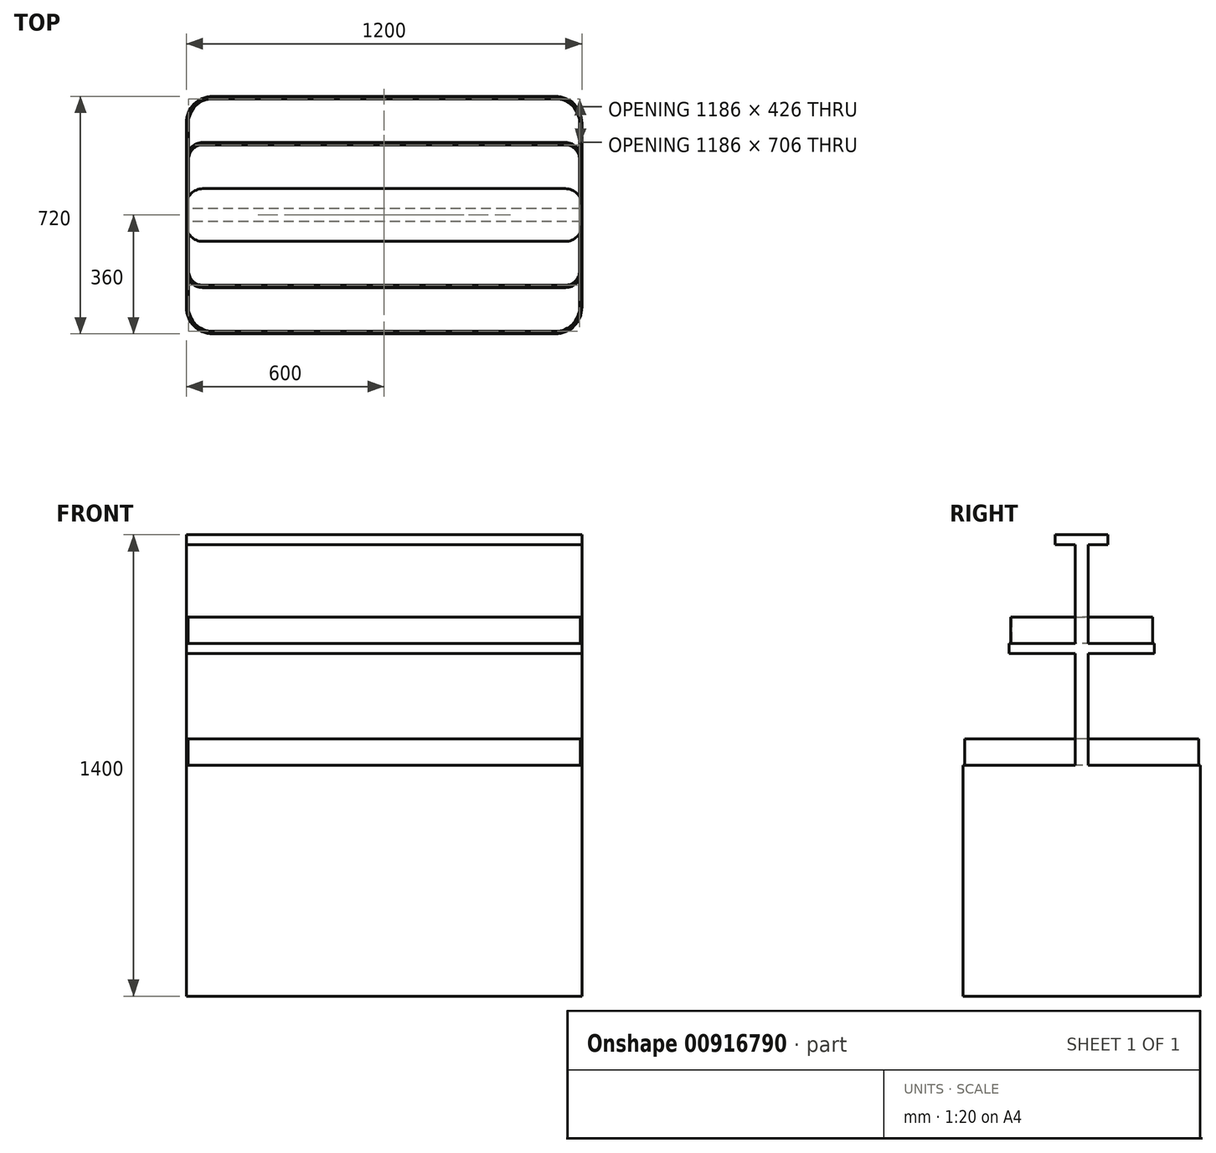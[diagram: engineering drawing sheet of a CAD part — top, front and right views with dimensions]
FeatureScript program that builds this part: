
annotation { "Feature Type Name" : "Feature", "Feature Type Description" : "" }
export const myFeature = defineFeature(function(context is Context, id is Id, definition is map)
    precondition{}
    {
        {
            var Q0;
            Q0=qCreatedBy(makeId("Front.planeOp"),FACE);
            var sketch = newSketch(context, id + "F0", { "sketchPlane" : qUnion([Q0])});
            skLineSegment(sketch, "E0.bottom", {"start": v(-600, 0) * mm, "end": v(600, 0) * mm});
            skLineSegment(sketch, "E0.top", {"start": v(-600, 1400) * mm, "end": v(600, 1400) * mm});
            skLineSegment(sketch, "E0.left", {"start": v(-600, 0) * mm, "end": v(-600, 1400) * mm});
            skLineSegment(sketch, "E0.right", {"start": v(600, 0) * mm, "end": v(600, 1400) * mm});
            skLineSegment(sketch, "E1", {"start": v(-600, 150) * mm, "end": v(600, 150) * mm});
            skLineSegment(sketch, "E2", {"start": v(-600, 700) * mm, "end": v(600, 700) * mm});
            skLineSegment(sketch, "E3", {"start": v(-600, 1370) * mm, "end": v(600, 1370) * mm});
            skLineSegment(sketch, "E4", {"start": v(-600, 1040) * mm, "end": v(600, 1040) * mm});
            skLineSegment(sketch, "E5", {"start": v(-600, 1070) * mm, "end": v(600, 1070) * mm});
            skSolve(sketch);
        }
        {
            var Q0;
            Q0=qCreatedBy(makeId("Top.planeOp"),FACE);
            var sketch = newSketch(context, id + "F1", { "sketchPlane" : qUnion([Q0])});
            skLineSegment(sketch, "E6.bottom", {"start": v(600, 360) * mm, "end": v(-600, 360) * mm});
            skLineSegment(sketch, "E6.top", {"start": v(600, -360) * mm, "end": v(-600, -360) * mm});
            skLineSegment(sketch, "E6.left", {"start": v(600, 360) * mm, "end": v(600, -360) * mm});
            skLineSegment(sketch, "E6.right", {"start": v(-600, 360) * mm, "end": v(-600, -360) * mm});
            skPoint(sketch, "E6.middle", {"position": v(0, 0) * mm});
            skLineSegment(sketch, "E7.bottom", {"start": v(600, 20) * mm, "end": v(-600, 20) * mm});
            skLineSegment(sketch, "E7.top", {"start": v(600, -20) * mm, "end": v(-600, -20) * mm});
            skLineSegment(sketch, "E7.left", {"start": v(600, 20) * mm, "end": v(600, -20) * mm});
            skLineSegment(sketch, "E7.right", {"start": v(-600, 20) * mm, "end": v(-600, -20) * mm});
            skLineSegment(sketch, "E8", {"start": v(-600, 220) * mm, "end": v(600, 220) * mm});
            skLineSegment(sketch, "E9", {"start": v(-600, -220) * mm, "end": v(600, -220) * mm});
            skLineSegment(sketch, "E10.0", {"start": v(550, 310) * mm, "end": v(-550, 310) * mm});
            skLineSegment(sketch, "E10.1", {"start": v(550, 310) * mm, "end": v(550, -310) * mm});
            skLineSegment(sketch, "E10.2", {"start": v(550, -310) * mm, "end": v(-550, -310) * mm});
            skLineSegment(sketch, "E10.3", {"start": v(-550, 310) * mm, "end": v(-550, -310) * mm});
            skLineSegment(sketch, "E11", {"start": v(-600, -80) * mm, "end": v(600, -80) * mm});
            skLineSegment(sketch, "E12", {"start": v(-600, 80) * mm, "end": v(600, 80) * mm});
            skSolve(sketch);
        }
        {
            var Q0;
            Q0=qCreatedBy(makeId("Top.planeOp"),FACE);
            var sketch = newSketch(context, id + "F2", { "sketchPlane" : qUnion([Q0])});
            skLineSegment(sketch, "E13.0", {"start": v(550, 310) * mm, "end": v(-550, 310) * mm});
            skLineSegment(sketch, "E13.1", {"start": v(-550, 310) * mm, "end": v(-550, -310) * mm});
            skLineSegment(sketch, "E13.2", {"start": v(550, -310) * mm, "end": v(-550, -310) * mm});
            skLineSegment(sketch, "E13.3", {"start": v(550, 310) * mm, "end": v(550, -310) * mm});
            skSolve(sketch);
        }
        {
            var Q0;
            Q0=qSketchRegion(id+"F2",true);
            var Q1;
            Q1=sQuery(id+"F0.wireOp",VERTEX,"E1.end");
            extrude(context, id + "F3", {"entities" : qUnion([Q0]), "endBound" : BoundingType.UP_TO_VERTEX, "depth" : 25 * mm, "endBoundEntityVertex" : qUnion([Q1]), "offsetDistance" : 25 * mm});
        }
        {
            var Q0;
            Q0=makeQuery(id+"F3.opExtrude","CAP_FACE",FACE,{"disambiguationData":[OSD([sQuery(id+"F2.wireOp",EDGE,"E13.0"),sQuery(id+"F2.wireOp",EDGE,"E13.1"),sQuery(id+"F2.wireOp",EDGE,"E13.2"),sQuery(id+"F2.wireOp",EDGE,"E13.3")])],"isStart":false});
            var sketch = newSketch(context, id + "F4", { "sketchPlane" : qUnion([Q0])});
            skLineSegment(sketch, "E14.0", {"start": v(600, 360) * mm, "end": v(-600, 360) * mm});
            skLineSegment(sketch, "E14.1", {"start": v(-600, 360) * mm, "end": v(-600, -360) * mm});
            skLineSegment(sketch, "E14.2", {"start": v(600, -360) * mm, "end": v(-600, -360) * mm});
            skLineSegment(sketch, "E14.3", {"start": v(600, 360) * mm, "end": v(600, -360) * mm});
            skSolve(sketch);
        }
        {
            var Q0;
            Q0=qSketchRegion(id+"F4",true);
            var Q1;
            Q1=sQuery(id+"F0.wireOp",VERTEX,"E2.end");
            extrude(context, id + "F5", {"entities" : qUnion([Q0]), "operationType" : NewBodyOperationType.ADD, "endBound" : BoundingType.UP_TO_VERTEX, "depth" : 25 * mm, "endBoundEntityVertex" : qUnion([Q1]), "offsetDistance" : 25 * mm});
        }
        {
            var Q0;
            Q0=makeQuery(id+"F5.opExtrude","CAP_FACE",FACE,{"disambiguationData":[OSD([sQuery(id+"F4.wireOp",EDGE,"E14.0"),sQuery(id+"F4.wireOp",EDGE,"E14.1"),sQuery(id+"F4.wireOp",EDGE,"E14.2"),sQuery(id+"F4.wireOp",EDGE,"E14.3")])],"isStart":false});
            var sketch = newSketch(context, id + "F6", { "sketchPlane" : qUnion([Q0])});
            skLineSegment(sketch, "E15.0", {"start": v(600, 20) * mm, "end": v(-600, 20) * mm});
            skLineSegment(sketch, "E15.1", {"start": v(600, -20) * mm, "end": v(-600, -20) * mm});
            skLineSegment(sketch, "E15.2", {"start": v(-600, 20) * mm, "end": v(-600, -20) * mm});
            skLineSegment(sketch, "E15.3", {"start": v(600, 20) * mm, "end": v(600, -20) * mm});
            skPoint(sketch, "E16.orphan", {"position": v(-600, 360) * mm});
            skPoint(sketch, "E17.orphan", {"position": v(-600, -360) * mm});
            skPoint(sketch, "E18.orphan", {"position": v(600, 360) * mm});
            skPoint(sketch, "E19.orphan", {"position": v(600, -360) * mm});
            skSolve(sketch);
        }
        {
            var Q0;
            Q0=qSketchRegion(id+"F6",true);
            var Q1;
            Q1=sQuery(id+"F0.wireOp",VERTEX,"E0.top.start");
            extrude(context, id + "F7", {"entities" : qUnion([Q0]), "operationType" : NewBodyOperationType.ADD, "endBound" : BoundingType.UP_TO_VERTEX, "depth" : 25 * mm, "endBoundEntityVertex" : qUnion([Q1]), "offsetDistance" : 25 * mm});
        }
        {
            var Q0;
            Q0=qCreatedBy(makeId("Top.planeOp"),FACE);
            var Q1;
            Q1=sQuery(id+"F0.wireOp",VERTEX,"E4.start");
            cPlane(context, id + "F8", {"entities" : qUnion([Q0, Q1]), "cplaneType" : CPlaneType.PLANE_POINT, "offset" : 25 * mm, "width" : 150 * mm, "height" : 150 * mm});
        }
        {
            var Q0;
            Q0=qCreatedBy(id+"F8.planeOp",FACE);
            var sketch = newSketch(context, id + "F9", { "sketchPlane" : qUnion([Q0])});
            skLineSegment(sketch, "E20.0", {"start": v(-600, 220) * mm, "end": v(600, 220) * mm});
            skLineSegment(sketch, "E20.1", {"start": v(-600, -220) * mm, "end": v(600, -220) * mm});
            skLineSegment(sketch, "E21", {"start": v(-600, 220) * mm, "end": v(-600, -220) * mm});
            skLineSegment(sketch, "E22", {"start": v(600, -220) * mm, "end": v(600, 220) * mm});
            skSolve(sketch);
        }
        {
            var Q0;
            Q0=qSketchRegion(id+"F9",true);
            var Q1;
            Q1=sQuery(id+"F0.wireOp",VERTEX,"E5.start");
            extrude(context, id + "F10", {"entities" : qUnion([Q0]), "operationType" : NewBodyOperationType.ADD, "endBound" : BoundingType.UP_TO_VERTEX, "depth" : 25 * mm, "endBoundEntityVertex" : qUnion([Q1]), "offsetDistance" : 25 * mm});
        }
        {
            var Q0;
            Q0=makeQuery(id+"F7.opExtrude","CAP_FACE",FACE,{"disambiguationData":[OSD([sQuery(id+"F6.wireOp",EDGE,"E15.0"),sQuery(id+"F6.wireOp",EDGE,"E15.1"),sQuery(id+"F6.wireOp",EDGE,"E15.2"),sQuery(id+"F6.wireOp",EDGE,"E15.3")])],"isStart":false});
            var sketch = newSketch(context, id + "F11", { "sketchPlane" : qUnion([Q0])});
            skLineSegment(sketch, "E23.0", {"start": v(-600, -80) * mm, "end": v(600, -80) * mm});
            skLineSegment(sketch, "E23.1", {"start": v(-600, 80) * mm, "end": v(600, 80) * mm});
            skLineSegment(sketch, "E24", {"start": v(-600, -80) * mm, "end": v(-600, 80) * mm});
            skLineSegment(sketch, "E25", {"start": v(600, -80) * mm, "end": v(600, 80) * mm});
            skSolve(sketch);
        }
        {
            var Q0;
            Q0=qSketchRegion(id+"F11",true);
            var Q1;
            Q1=sQuery(id+"F0.wireOp",VERTEX,"E3.start");
            extrude(context, id + "F12", {"entities" : qUnion([Q0]), "operationType" : NewBodyOperationType.ADD, "endBound" : BoundingType.UP_TO_VERTEX, "oppositeDirection" : true, "depth" : 25 * mm, "endBoundEntityVertex" : qUnion([Q1]), "offsetDistance" : 25 * mm});
        }
        {
            var Q0;
            Q0=makeQuery(id+"F5.opExtrude","SWEPT_EDGE",EDGE,{"disambiguationData":[OSD([sQuery(id+"F4.wireOp",EDGE,"E14.2"),sQuery(id+"F4.wireOp",EDGE,"E14.3")])]});
            var Q1;
            Q1=makeQuery(id+"F5.opExtrude","SWEPT_EDGE",EDGE,{"disambiguationData":[OSD([sQuery(id+"F4.wireOp",EDGE,"E14.1"),sQuery(id+"F4.wireOp",EDGE,"E14.2")])]});
            var Q2;
            Q2=makeQuery(id+"F5.opExtrude","SWEPT_EDGE",EDGE,{"disambiguationData":[OSD([sQuery(id+"F4.wireOp",EDGE,"E14.0"),sQuery(id+"F4.wireOp",EDGE,"E14.3")])]});
            var Q3;
            Q3=makeQuery(id+"F5.opExtrude","SWEPT_EDGE",EDGE,{"disambiguationData":[OSD([sQuery(id+"F4.wireOp",EDGE,"E14.0"),sQuery(id+"F4.wireOp",EDGE,"E14.1")])]});
            fillet(context, id + "F13", {"entities" : qUnion([Q0, Q1, Q2, Q3]), "radius" : 80 * mm, "tangentPropagation" : true, "allowEdgeOverflow" : false});
        }
        {
            var Q0;
            Q0=makeQuery(id+"F3.opExtrude","SWEPT_EDGE",EDGE,{"disambiguationData":[OSD([sQuery(id+"F2.wireOp",EDGE,"E13.0"),sQuery(id+"F2.wireOp",EDGE,"E13.1")])]});
            var Q1;
            Q1=makeQuery(id+"F3.opExtrude","SWEPT_EDGE",EDGE,{"disambiguationData":[OSD([sQuery(id+"F2.wireOp",EDGE,"E13.1"),sQuery(id+"F2.wireOp",EDGE,"E13.2")])]});
            var Q2;
            Q2=makeQuery(id+"F3.opExtrude","SWEPT_EDGE",EDGE,{"disambiguationData":[OSD([sQuery(id+"F2.wireOp",EDGE,"E13.2"),sQuery(id+"F2.wireOp",EDGE,"E13.3")])]});
            var Q3;
            Q3=makeQuery(id+"F3.opExtrude","SWEPT_EDGE",EDGE,{"disambiguationData":[OSD([sQuery(id+"F2.wireOp",EDGE,"E13.0"),sQuery(id+"F2.wireOp",EDGE,"E13.3")])]});
            fillet(context, id + "F14", {"entities" : qUnion([Q0, Q1, Q2, Q3]), "radius" : 85 * mm, "tangentPropagation" : true, "allowEdgeOverflow" : false});
        }
        {
            var Q0;
            Q0=makeQuery(id+"F10.opExtrude","SWEPT_EDGE",EDGE,{"disambiguationData":[OSD([sQuery(id+"F9.wireOp",EDGE,"E20.0"),sQuery(id+"F9.wireOp",EDGE,"E22")])]});
            var Q1;
            Q1=makeQuery(id+"F10.opExtrude","SWEPT_EDGE",EDGE,{"disambiguationData":[OSD([sQuery(id+"F9.wireOp",EDGE,"E20.0"),sQuery(id+"F9.wireOp",EDGE,"E21")])]});
            var Q2;
            Q2=makeQuery(id+"F10.opExtrude","SWEPT_EDGE",EDGE,{"disambiguationData":[OSD([sQuery(id+"F9.wireOp",EDGE,"E20.1"),sQuery(id+"F9.wireOp",EDGE,"E21")])]});
            var Q3;
            Q3=makeQuery(id+"F10.opExtrude","SWEPT_EDGE",EDGE,{"disambiguationData":[OSD([sQuery(id+"F9.wireOp",EDGE,"E20.1"),sQuery(id+"F9.wireOp",EDGE,"E22")])]});
            fillet(context, id + "F15", {"entities" : qUnion([Q0, Q1, Q2, Q3]), "radius" : 50 * mm, "tangentPropagation" : true, "allowEdgeOverflow" : false});
        }
        {
            var Q0;
            Q0=makeQuery(id+"F12.opExtrude","SWEPT_EDGE",EDGE,{"disambiguationData":[OSD([sQuery(id+"F11.wireOp",EDGE,"E23.0"),sQuery(id+"F11.wireOp",EDGE,"E25")])]});
            var Q1;
            Q1=makeQuery(id+"F12.opExtrude","SWEPT_EDGE",EDGE,{"disambiguationData":[OSD([sQuery(id+"F11.wireOp",EDGE,"E23.1"),sQuery(id+"F11.wireOp",EDGE,"E25")])]});
            var Q2;
            Q2=makeQuery(id+"F12.opExtrude","SWEPT_EDGE",EDGE,{"disambiguationData":[OSD([sQuery(id+"F11.wireOp",EDGE,"E23.0"),sQuery(id+"F11.wireOp",EDGE,"E24")])]});
            var Q3;
            Q3=makeQuery(id+"F12.opExtrude","SWEPT_EDGE",EDGE,{"disambiguationData":[OSD([sQuery(id+"F11.wireOp",EDGE,"E23.1"),sQuery(id+"F11.wireOp",EDGE,"E24")])]});
            fillet(context, id + "F16", {"entities" : qUnion([Q0, Q1, Q2, Q3]), "radius" : 50 * mm, "tangentPropagation" : true, "allowEdgeOverflow" : false});
        }
        {
            var Q0;
            {var subQ0=sQuery(id+"F4.wireOp",EDGE,"E14.3");var subQ1=sQuery(id+"F4.wireOp",EDGE,"E14.2");var subQ2=sQuery(id+"F4.wireOp",EDGE,"E14.1");Q0=makeQuery(id+"F7.boolean.opBoolean","SPLIT",FACE,{"disambiguationData":[TD([makeQuery(id+"F5.opExtrude","SWEPT_FACE",FACE,{"disambiguationData":[OSD([subQ1])]})])],"derivedFrom":makeQuery(id+"F5.opExtrude","CAP_FACE",FACE,{"disambiguationData":[OSD([sQuery(id+"F4.wireOp",EDGE,"E14.0"),subQ2,subQ1,subQ0])],"isStart":false})});}
            var sketch = newSketch(context, id + "F17", { "sketchPlane" : qUnion([Q0])});
            skArc(sketch, "E26.0", {"start": v(-595, 280) * mm, "mid": v(-573.03, 333.03) * mm, "end": v(-520, 355) * mm});
            skLineSegment(sketch, "E26.1", {"start": v(520, 355) * mm, "end": v(-520, 355) * mm});
            skLineSegment(sketch, "E26.2", {"start": v(-595, 280) * mm, "end": v(-595, -280) * mm});
            skArc(sketch, "E26.3", {"start": v(520, 355) * mm, "mid": v(573.03, 333.03) * mm, "end": v(595, 280) * mm});
            skArc(sketch, "E26.4", {"start": v(-520, -355) * mm, "mid": v(-573.03, -333.03) * mm, "end": v(-595, -280) * mm});
            skLineSegment(sketch, "E26.5", {"start": v(520, -355) * mm, "end": v(-520, -355) * mm});
            skArc(sketch, "E26.6", {"start": v(595, -280) * mm, "mid": v(573.03, -333.03) * mm, "end": v(520, -355) * mm});
            skLineSegment(sketch, "E26.7", {"start": v(595, 280) * mm, "end": v(595, -280) * mm});
            skLineSegment(sketch, "E27.0", {"start": v(520, -353) * mm, "end": v(-520, -353) * mm});
            skArc(sketch, "E27.1", {"start": v(593, -280) * mm, "mid": v(571.62, -331.62) * mm, "end": v(520, -353) * mm});
            skArc(sketch, "E27.2", {"start": v(-520, -353) * mm, "mid": v(-571.62, -331.62) * mm, "end": v(-593, -280) * mm});
            skLineSegment(sketch, "E27.3", {"start": v(593, 280) * mm, "end": v(593, -280) * mm});
            skLineSegment(sketch, "E27.4", {"start": v(-593, 280) * mm, "end": v(-593, -280) * mm});
            skArc(sketch, "E27.5", {"start": v(-593, 280) * mm, "mid": v(-571.62, 331.62) * mm, "end": v(-520, 353) * mm});
            skLineSegment(sketch, "E27.6", {"start": v(520, 353) * mm, "end": v(-520, 353) * mm});
            skArc(sketch, "E27.7", {"start": v(520, 353) * mm, "mid": v(571.62, 331.62) * mm, "end": v(593, 280) * mm});
            skSolve(sketch);
        }
        {
            var Q0;
            Q0=qSketchRegion(id+"F17",true);
            extrude(context, id + "F18", {"entities" : qUnion([Q0]), "depth" : 80 * mm, "offsetDistance" : 25 * mm});
        }
        {
            var Q0;
            {var subQ0=sQuery(id+"F9.wireOp",EDGE,"E20.1");var subQ1=sQuery(id+"F9.wireOp",EDGE,"E21");var subQ2=sQuery(id+"F9.wireOp",EDGE,"E22");Q0=makeQuery(id+"F10.boolean.opBoolean","SPLIT",FACE,{"disambiguationData":[TD([makeQuery(id+"F7.opExtrude","SWEPT_FACE",FACE,{"disambiguationData":[OSD([sQuery(id+"F6.wireOp",EDGE,"E15.1")])]})])],"derivedFrom":makeQuery(id+"F10.opExtrude","CAP_FACE",FACE,{"disambiguationData":[OSD([sQuery(id+"F9.wireOp",EDGE,"E20.0"),subQ0,subQ1,subQ2])],"isStart":false})});}
            var sketch = newSketch(context, id + "F19", { "sketchPlane" : qUnion([Q0])});
            skLineSegment(sketch, "E28.0", {"start": v(-595, 170) * mm, "end": v(-595, 15) * mm});
            skLineSegment(sketch, "E28.1", {"start": v(595, 15) * mm, "end": v(595, 170) * mm});
            skArc(sketch, "E28.2", {"start": v(595, 170) * mm, "mid": v(581.82, 201.82) * mm, "end": v(550, 215) * mm});
            skLineSegment(sketch, "E28.3", {"start": v(-550, 215) * mm, "end": v(550, 215) * mm});
            skArc(sketch, "E28.4", {"start": v(-550, 215) * mm, "mid": v(-581.82, 201.82) * mm, "end": v(-595, 170) * mm});
            skLineSegment(sketch, "E29.0", {"start": v(595, -170) * mm, "end": v(595, -15) * mm});
            skLineSegment(sketch, "E29.1", {"start": v(-595, -15) * mm, "end": v(-595, -170) * mm});
            skArc(sketch, "E29.2", {"start": v(-595, -170) * mm, "mid": v(-581.82, -201.82) * mm, "end": v(-550, -215) * mm});
            skLineSegment(sketch, "E29.3", {"start": v(-550, -215) * mm, "end": v(550, -215) * mm});
            skArc(sketch, "E29.4", {"start": v(550, -215) * mm, "mid": v(581.82, -201.82) * mm, "end": v(595, -170) * mm});
            skLineSegment(sketch, "E30", {"start": v(-595, 15) * mm, "end": v(-595, -15) * mm});
            skLineSegment(sketch, "E31", {"start": v(595, 15) * mm, "end": v(595, -15) * mm});
            skLineSegment(sketch, "E32.0", {"start": v(593, 15) * mm, "end": v(593, 170) * mm});
            skLineSegment(sketch, "E32.1", {"start": v(-593, 15) * mm, "end": v(-593, -15) * mm});
            skLineSegment(sketch, "E32.2", {"start": v(-593, 170) * mm, "end": v(-593, 15) * mm});
            skArc(sketch, "E32.3", {"start": v(-550, 213) * mm, "mid": v(-580.4, 200.4) * mm, "end": v(-593, 170) * mm});
            skLineSegment(sketch, "E32.4", {"start": v(-550, 213) * mm, "end": v(550, 213) * mm});
            skLineSegment(sketch, "E32.5", {"start": v(-593, -15) * mm, "end": v(-593, -170) * mm});
            skArc(sketch, "E32.6", {"start": v(593, 170) * mm, "mid": v(580.4, 200.4) * mm, "end": v(550, 213) * mm});
            skArc(sketch, "E32.7", {"start": v(-593, -170) * mm, "mid": v(-580.4, -200.4) * mm, "end": v(-550, -213) * mm});
            skLineSegment(sketch, "E32.8", {"start": v(-550, -213) * mm, "end": v(550, -213) * mm});
            skArc(sketch, "E32.9", {"start": v(550, -213) * mm, "mid": v(580.4, -200.4) * mm, "end": v(593, -170) * mm});
            skLineSegment(sketch, "E32.10", {"start": v(593, -170) * mm, "end": v(593, -15) * mm});
            skLineSegment(sketch, "E32.11", {"start": v(593, 15) * mm, "end": v(593, -15) * mm});
            skSolve(sketch);
        }
        {
            var Q0;
            Q0=qSketchRegion(id+"F19",true);
            extrude(context, id + "F20", {"entities" : qUnion([Q0]), "depth" : 80 * mm, "offsetDistance" : 25 * mm});
        }
        {
            var Q0;
            Q0=makeQuery(id+"F12.boolean.opBoolean","MERGE",FACE,{"derivedFrom":[makeQuery(id+"F10.boolean.opBoolean","MERGE",FACE,{"derivedFrom":[makeQuery(id+"F7.boolean.opBoolean","MERGE",FACE,{"derivedFrom":[makeQuery(id+"F5.opExtrude","SWEPT_FACE",FACE,{"disambiguationData":[OSD([sQuery(id+"F4.wireOp",EDGE,"E14.3")])]}),makeQuery(id+"F7.opExtrude","SWEPT_FACE",FACE,{"disambiguationData":[OSD([sQuery(id+"F6.wireOp",EDGE,"E15.3")])]})]}),makeQuery(id+"F10.opExtrude","SWEPT_FACE",FACE,{"disambiguationData":[OSD([sQuery(id+"F9.wireOp",EDGE,"E22")])]})]}),makeQuery(id+"F12.opExtrude","SWEPT_FACE",FACE,{"disambiguationData":[OSD([sQuery(id+"F11.wireOp",EDGE,"E25")])]})]});
            var sketch = newSketch(context, id + "F21", { "sketchPlane" : qUnion([Q0])});
            skLineSegment(sketch, "E33", {"start": v(0, 0) * mm, "end": v(0, 2000) * mm, "construction": true});
            skLineSegment(sketch, "E34", {"start": v(0, 2000) * mm, "end": v(-360, 1950) * mm});
            skLineSegment(sketch, "E35", {"start": v(-360, 1950) * mm, "end": v(-360, 1800) * mm});
            skLineSegment(sketch, "E36.MirrorCS", {"start": v(0, 2000) * mm, "end": v(360, 1950) * mm});
            skLineSegment(sketch, "E37.MirrorCS", {"start": v(360, 1950) * mm, "end": v(360, 1800) * mm});
            skSolve(sketch);
        }
        {
            var Q0;
            {var subQ6=sQuery(id+"F4.wireOp",EDGE,"E14.3");Q0=makeQuery(id+"F21.imprint","IMPRINT",FACE,{"disambiguationData":[TD([[makeQuery(id+"F21.imprint","IMPRINT",EDGE,{"derivedFrom":makeQuery(id+"F5.opExtrude","CAP_EDGE",EDGE,{"disambiguationData":[OSD([subQ6])],"isStart":true})}),-1.0]])]});}
            var sketch = newSketch(context, id + "F22", { "sketchPlane" : qUnion([Q0])});
            skLineSegment(sketch, "E38.0", {"start": v(0, 2000) * mm, "end": v(-360, 1950) * mm});
            skLineSegment(sketch, "E38.1", {"start": v(0, 2000) * mm, "end": v(360, 1950) * mm});
            skLineSegment(sketch, "E39.0", {"start": v(0, 1994.95) * mm, "end": v(-359.3, 1945.05) * mm});
            skLineSegment(sketch, "E39.1", {"start": v(0, 1994.95) * mm, "end": v(359.3, 1945.05) * mm});
            skLineSegment(sketch, "E40", {"start": v(-360, 1950) * mm, "end": v(-359.3, 1945.05) * mm});
            skLineSegment(sketch, "E41", {"start": v(359.3, 1945.05) * mm, "end": v(360, 1950) * mm});
            skSolve(sketch);
        }
        {
            var Q0;
            Q0=qSketchRegion(id+"F22",true);
            var Q1;
            Q1=makeQuery(id+"F12.boolean.opBoolean","MERGE",FACE,{"derivedFrom":[makeQuery(id+"F10.boolean.opBoolean","MERGE",FACE,{"derivedFrom":[makeQuery(id+"F7.boolean.opBoolean","MERGE",FACE,{"derivedFrom":[makeQuery(id+"F5.opExtrude","SWEPT_FACE",FACE,{"disambiguationData":[OSD([sQuery(id+"F4.wireOp",EDGE,"E14.1")])]}),makeQuery(id+"F7.opExtrude","SWEPT_FACE",FACE,{"disambiguationData":[OSD([sQuery(id+"F6.wireOp",EDGE,"E15.2")])]})]}),makeQuery(id+"F10.opExtrude","SWEPT_FACE",FACE,{"disambiguationData":[OSD([sQuery(id+"F9.wireOp",EDGE,"E21")])]})]}),makeQuery(id+"F12.opExtrude","SWEPT_FACE",FACE,{"disambiguationData":[OSD([sQuery(id+"F11.wireOp",EDGE,"E24")])]})]});
            extrude(context, id + "F23", {"entities" : qUnion([Q0]), "endBound" : BoundingType.UP_TO_SURFACE, "oppositeDirection" : true, "depth" : 2960 * mm, "endBoundEntityFace" : qUnion([Q1]), "offsetDistance" : 25 * mm});
        }
        {
            var Q0;
            Q0=makeQuery(id+"F5.opExtrude","SWEPT_FACE",FACE,{"disambiguationData":[OSD([sQuery(id+"F4.wireOp",EDGE,"E14.2")])]});
            var sketch = newSketch(context, id + "F24", { "sketchPlane" : qUnion([Q0])});
            skLineSegment(sketch, "E42.0", {"start": v(-600, 1950) * mm, "end": v(600, 1950) * mm});
            skLineSegment(sketch, "E43", {"start": v(-600, 1950) * mm, "end": v(-600, 1860) * mm});
            skArc(sketch, "E44", {"start": v(-600, 1860) * mm, "mid": v(-540, 1800) * mm, "end": v(-480, 1860) * mm});
            skArc(sketch, "E45.1.0.0", {"start": v(-480, 1860) * mm, "mid": v(-420, 1800) * mm, "end": v(-360, 1860) * mm});
            skArc(sketch, "E45.2.0.0", {"start": v(-360, 1860) * mm, "mid": v(-300, 1800) * mm, "end": v(-240, 1860) * mm});
            skArc(sketch, "E45.3.0.0", {"start": v(-240, 1860) * mm, "mid": v(-180, 1800) * mm, "end": v(-120, 1860) * mm});
            skArc(sketch, "E45.4.0.0", {"start": v(-120, 1860) * mm, "mid": v(-60, 1800) * mm, "end": v(0, 1860) * mm});
            skArc(sketch, "E45.5.0.0", {"start": v(0, 1860) * mm, "mid": v(60, 1800) * mm, "end": v(120, 1860) * mm});
            skArc(sketch, "E45.6.0.0", {"start": v(120, 1860) * mm, "mid": v(180, 1800) * mm, "end": v(240, 1860) * mm});
            skArc(sketch, "E45.7.0.0", {"start": v(240, 1860) * mm, "mid": v(300, 1800) * mm, "end": v(360, 1860) * mm});
            skArc(sketch, "E45.8.0.0", {"start": v(360, 1860) * mm, "mid": v(420, 1800) * mm, "end": v(480, 1860) * mm});
            skArc(sketch, "E45.9.0.0", {"start": v(480, 1860) * mm, "mid": v(540, 1800) * mm, "end": v(600, 1860) * mm});
            skLineSegment(sketch, "E45.direction1", {"start": v(-600, 1860) * mm, "end": v(-480, 1860) * mm, "construction": true});
            skLineSegment(sketch, "E46", {"start": v(600, 1950) * mm, "end": v(600, 1860) * mm});
            skSolve(sketch);
        }
        {
            var Q0;
            Q0=qSketchRegion(id+"F24",true);
            extrude(context, id + "F25", {"entities" : qUnion([Q0]), "operationType" : NewBodyOperationType.ADD, "oppositeDirection" : true, "depth" : 5 * mm, "offsetDistance" : 25 * mm});
        }
        {
            var Q0;
            Q0=makeQuery(id+"F5.opExtrude","SWEPT_FACE",FACE,{"disambiguationData":[OSD([sQuery(id+"F4.wireOp",EDGE,"E14.0")])]});
            var sketch = newSketch(context, id + "F26", { "sketchPlane" : qUnion([Q0])});
            skLineSegment(sketch, "E47.0", {"start": v(600, 1950) * mm, "end": v(-600, 1950) * mm});
            skLineSegment(sketch, "E48", {"start": v(-600, 1950) * mm, "end": v(-600, 1860) * mm});
            skArc(sketch, "E49", {"start": v(-600, 1860) * mm, "mid": v(-540, 1800) * mm, "end": v(-480, 1860) * mm});
            skArc(sketch, "E50.1.0.0", {"start": v(-480, 1860) * mm, "mid": v(-420, 1800) * mm, "end": v(-360, 1860) * mm});
            skArc(sketch, "E50.2.0.0", {"start": v(-360, 1860) * mm, "mid": v(-300, 1800) * mm, "end": v(-240, 1860) * mm});
            skArc(sketch, "E50.3.0.0", {"start": v(-240, 1860) * mm, "mid": v(-180, 1800) * mm, "end": v(-120, 1860) * mm});
            skArc(sketch, "E50.4.0.0", {"start": v(-120, 1860) * mm, "mid": v(-60, 1800) * mm, "end": v(0, 1860) * mm});
            skArc(sketch, "E50.5.0.0", {"start": v(0, 1860) * mm, "mid": v(60, 1800) * mm, "end": v(120, 1860) * mm});
            skArc(sketch, "E50.6.0.0", {"start": v(120, 1860) * mm, "mid": v(180, 1800) * mm, "end": v(240, 1860) * mm});
            skArc(sketch, "E50.7.0.0", {"start": v(240, 1860) * mm, "mid": v(300, 1800) * mm, "end": v(360, 1860) * mm});
            skArc(sketch, "E50.8.0.0", {"start": v(360, 1860) * mm, "mid": v(420, 1800) * mm, "end": v(480, 1860) * mm});
            skArc(sketch, "E50.9.0.0", {"start": v(480, 1860) * mm, "mid": v(540, 1800) * mm, "end": v(600, 1860) * mm});
            skLineSegment(sketch, "E50.direction1", {"start": v(-600, 1860) * mm, "end": v(-480, 1860) * mm, "construction": true});
            skLineSegment(sketch, "E51", {"start": v(600, 1950) * mm, "end": v(600, 1860) * mm});
            skSolve(sketch);
        }
        {
            var Q0;
            Q0=qSketchRegion(id+"F26",true);
            extrude(context, id + "F27", {"entities" : qUnion([Q0]), "operationType" : NewBodyOperationType.ADD, "oppositeDirection" : true, "depth" : 5 * mm, "offsetDistance" : 25 * mm});
        }
        {
            var Q0;
            Q0=makeQuery(id+"F12.boolean.opBoolean","MERGE",FACE,{"derivedFrom":[makeQuery(id+"F10.boolean.opBoolean","MERGE",FACE,{"derivedFrom":[makeQuery(id+"F7.boolean.opBoolean","MERGE",FACE,{"derivedFrom":[makeQuery(id+"F5.opExtrude","SWEPT_FACE",FACE,{"disambiguationData":[OSD([sQuery(id+"F4.wireOp",EDGE,"E14.3")])]}),makeQuery(id+"F7.opExtrude","SWEPT_FACE",FACE,{"disambiguationData":[OSD([sQuery(id+"F6.wireOp",EDGE,"E15.3")])]})]}),makeQuery(id+"F10.opExtrude","SWEPT_FACE",FACE,{"disambiguationData":[OSD([sQuery(id+"F9.wireOp",EDGE,"E22")])]})]}),makeQuery(id+"F12.opExtrude","SWEPT_FACE",FACE,{"disambiguationData":[OSD([sQuery(id+"F11.wireOp",EDGE,"E25")])]})]});
            var sketch = newSketch(context, id + "F28", { "sketchPlane" : qUnion([Q0])});
            skLineSegment(sketch, "E52.0", {"start": v(0, 2000) * mm, "end": v(-360, 1950) * mm});
            skLineSegment(sketch, "E52.1", {"start": v(-360, 1860) * mm, "end": v(-360, 1950) * mm});
            skArc(sketch, "E53", {"start": v(-360, 1860) * mm, "mid": v(-300, 1800) * mm, "end": v(-240, 1860) * mm});
            skArc(sketch, "E54.1.0.0", {"start": v(-240, 1860) * mm, "mid": v(-180, 1800) * mm, "end": v(-120, 1860) * mm});
            skArc(sketch, "E54.2.0.0", {"start": v(-120, 1860) * mm, "mid": v(-60, 1800) * mm, "end": v(0, 1860) * mm});
            skArc(sketch, "E54.3.0.0", {"start": v(0, 1860) * mm, "mid": v(60, 1800) * mm, "end": v(120, 1860) * mm});
            skArc(sketch, "E54.4.0.0", {"start": v(120, 1860) * mm, "mid": v(180, 1800) * mm, "end": v(240, 1860) * mm});
            skArc(sketch, "E54.5.0.0", {"start": v(240, 1860) * mm, "mid": v(300, 1800) * mm, "end": v(360, 1860) * mm});
            skLineSegment(sketch, "E54.direction1", {"start": v(-360, 1860) * mm, "end": v(-240, 1860) * mm, "construction": true});
            skLineSegment(sketch, "E55.1", {"start": v(0, 2000) * mm, "end": v(360, 1950) * mm});
            skLineSegment(sketch, "E56", {"start": v(360, 1950) * mm, "end": v(360, 1860) * mm});
            skSolve(sketch);
        }
        {
            var Q0;
            Q0=makeQuery(id+"F28.imprint","IMPRINT",FACE,{"disambiguationData":[TD([[makeQuery(id+"F28.imprint","IMPRINT",EDGE,{"derivedFrom":sQuery(id+"F28.wireOp",EDGE,"E52.0")}),1.0]])]});
            extrude(context, id + "F29", {"entities" : qUnion([Q0]), "operationType" : NewBodyOperationType.ADD, "oppositeDirection" : true, "depth" : 5 * mm, "offsetDistance" : 25 * mm});
        }
        {
            var Q0;
            Q0=makeQuery(id+"F12.boolean.opBoolean","MERGE",FACE,{"derivedFrom":[makeQuery(id+"F10.boolean.opBoolean","MERGE",FACE,{"derivedFrom":[makeQuery(id+"F7.boolean.opBoolean","MERGE",FACE,{"derivedFrom":[makeQuery(id+"F5.opExtrude","SWEPT_FACE",FACE,{"disambiguationData":[OSD([sQuery(id+"F4.wireOp",EDGE,"E14.1")])]}),makeQuery(id+"F7.opExtrude","SWEPT_FACE",FACE,{"disambiguationData":[OSD([sQuery(id+"F6.wireOp",EDGE,"E15.2")])]})]}),makeQuery(id+"F10.opExtrude","SWEPT_FACE",FACE,{"disambiguationData":[OSD([sQuery(id+"F9.wireOp",EDGE,"E21")])]})]}),makeQuery(id+"F12.opExtrude","SWEPT_FACE",FACE,{"disambiguationData":[OSD([sQuery(id+"F11.wireOp",EDGE,"E24")])]})]});
            var sketch = newSketch(context, id + "F30", { "sketchPlane" : qUnion([Q0])});
            skArc(sketch, "E57", {"start": v(-360, 1860) * mm, "mid": v(-300, 1800) * mm, "end": v(-240, 1860) * mm});
            skArc(sketch, "E58.1.0.0", {"start": v(-240, 1860) * mm, "mid": v(-180, 1800) * mm, "end": v(-120, 1860) * mm});
            skArc(sketch, "E58.2.0.0", {"start": v(-120, 1860) * mm, "mid": v(-60, 1800) * mm, "end": v(0, 1860) * mm});
            skArc(sketch, "E58.3.0.0", {"start": v(0, 1860) * mm, "mid": v(60, 1800) * mm, "end": v(120, 1860) * mm});
            skArc(sketch, "E58.4.0.0", {"start": v(120, 1860) * mm, "mid": v(180, 1800) * mm, "end": v(240, 1860) * mm});
            skArc(sketch, "E58.5.0.0", {"start": v(240, 1860) * mm, "mid": v(300, 1800) * mm, "end": v(360, 1860) * mm});
            skLineSegment(sketch, "E58.direction1", {"start": v(-360, 1860) * mm, "end": v(-240, 1860) * mm, "construction": true});
            skLineSegment(sketch, "E59.0", {"start": v(360, 1950) * mm, "end": v(0, 2000) * mm});
            skLineSegment(sketch, "E59.1", {"start": v(360, 1950) * mm, "end": v(360, 1860) * mm});
            skLineSegment(sketch, "E60.0", {"start": v(-360, 1950) * mm, "end": v(0, 2000) * mm});
            skLineSegment(sketch, "E60.1", {"start": v(-360, 1950) * mm, "end": v(-360, 1860) * mm});
            skSolve(sketch);
        }
        {
            var Q0;
            Q0=qSketchRegion(id+"F30",true);
            extrude(context, id + "F31", {"entities" : qUnion([Q0]), "operationType" : NewBodyOperationType.ADD, "oppositeDirection" : true, "depth" : 5 * mm, "offsetDistance" : 25 * mm});
        }
        {
            var Q0;
            Q0=makeQuery(id+"F12.boolean.opBoolean","MERGE",FACE,{"derivedFrom":[makeQuery(id+"F7.opExtrude","CAP_FACE",FACE,{"disambiguationData":[OSD([sQuery(id+"F6.wireOp",EDGE,"E15.0"),sQuery(id+"F6.wireOp",EDGE,"E15.1"),sQuery(id+"F6.wireOp",EDGE,"E15.2"),sQuery(id+"F6.wireOp",EDGE,"E15.3")])],"isStart":false}),makeQuery(id+"F12.opExtrude","CAP_FACE",FACE,{"disambiguationData":[OSD([sQuery(id+"F11.wireOp",EDGE,"E23.0"),sQuery(id+"F11.wireOp",EDGE,"E23.1"),sQuery(id+"F11.wireOp",EDGE,"E24"),sQuery(id+"F11.wireOp",EDGE,"E25")])],"isStart":true})]});
            var sketch = newSketch(context, id + "F32", { "sketchPlane" : qUnion([Q0])});
            skCircle(sketch, "E61", {"center": v(-520, 0) * mm, "radius": 15 * mm});
            skLineSegment(sketch, "E62", {"start": v(0, 350.36) * mm, "end": v(0, -351.1) * mm, "construction": true});
            skCircle(sketch, "E63.MirrorC", {"center": v(520, 0) * mm, "radius": 15 * mm});
            skSolve(sketch);
        }
        {
            var Q0;
            Q0=qSketchRegion(id+"F32",true);
            extrude(context, id + "F33", {"entities" : qUnion([Q0]), "endBound" : BoundingType.UP_TO_NEXT, "depth" : 25 * mm, "offsetDistance" : 25 * mm});
        }
        {
            var Q0;
            Q0=makeQuery(id+"F5.opExtrude","CAP_FACE",FACE,{"disambiguationData":[OSD([sQuery(id+"F4.wireOp",EDGE,"E14.0"),sQuery(id+"F4.wireOp",EDGE,"E14.1"),sQuery(id+"F4.wireOp",EDGE,"E14.2"),sQuery(id+"F4.wireOp",EDGE,"E14.3")])],"isStart":true});
            var sketch = newSketch(context, id + "F34", { "sketchPlane" : qUnion([Q0])});
            skArc(sketch, "E64.0", {"start": v(-520, 360) * mm, "mid": v(-576.57, 336.57) * mm, "end": v(-600, 280) * mm});
            skLineSegment(sketch, "E64.1", {"start": v(520, 360) * mm, "end": v(-520, 360) * mm});
            skArc(sketch, "E64.2", {"start": v(600, 280) * mm, "mid": v(576.57, 336.57) * mm, "end": v(520, 360) * mm});
            skLineSegment(sketch, "E64.3", {"start": v(600, -280) * mm, "end": v(600, 280) * mm});
            skArc(sketch, "E64.4", {"start": v(520, -360) * mm, "mid": v(576.57, -336.57) * mm, "end": v(600, -280) * mm});
            skLineSegment(sketch, "E64.5", {"start": v(520, -360) * mm, "end": v(-520, -360) * mm});
            skArc(sketch, "E64.6", {"start": v(-600, -280) * mm, "mid": v(-576.57, -336.57) * mm, "end": v(-520, -360) * mm});
            skLineSegment(sketch, "E64.7", {"start": v(-600, -280) * mm, "end": v(-600, 280) * mm});
            skSolve(sketch);
        }
        {
            var Q0;
            Q0=qSketchRegion(id+"F34",true);
            var Q1;
            Q1=makeQuery(id+"F3.opExtrude","CAP_FACE",FACE,{"disambiguationData":[OSD([sQuery(id+"F2.wireOp",EDGE,"E13.0"),sQuery(id+"F2.wireOp",EDGE,"E13.1"),sQuery(id+"F2.wireOp",EDGE,"E13.2"),sQuery(id+"F2.wireOp",EDGE,"E13.3")])],"isStart":true});
            extrude(context, id + "F35", {"entities" : qUnion([Q0]), "operationType" : NewBodyOperationType.ADD, "endBound" : BoundingType.UP_TO_SURFACE, "depth" : 25 * mm, "endBoundEntityFace" : qUnion([Q1]), "offsetDistance" : 25 * mm});
        }
        {
            var Q0;
            Q0=makeQuery(id+"F33.opExtrude","SWEPT_BODY",BODY,{"disambiguationData":[OSD([sQuery(id+"F32.wireOp",EDGE,"E61")])]});
            var Q1;
            Q1=makeQuery(id+"F33.opExtrude","SWEPT_BODY",BODY,{"disambiguationData":[OSD([sQuery(id+"F32.wireOp",EDGE,"E63.MirrorC")])]});
            var Q2;
            Q2=makeQuery(id+"F23.opExtrude","SWEPT_BODY",BODY,{"disambiguationData":[OSD([sQuery(id+"F22.wireOp",EDGE,"E38.0"),sQuery(id+"F22.wireOp",EDGE,"E38.1"),sQuery(id+"F22.wireOp",EDGE,"E39.0"),sQuery(id+"F22.wireOp",EDGE,"E39.1"),sQuery(id+"F22.wireOp",EDGE,"E40"),sQuery(id+"F22.wireOp",EDGE,"E41")])]});
            deleteBodies(context, id + "F36", {"entities" : qUnion([Q0, Q1, Q2])});
        }
    });
